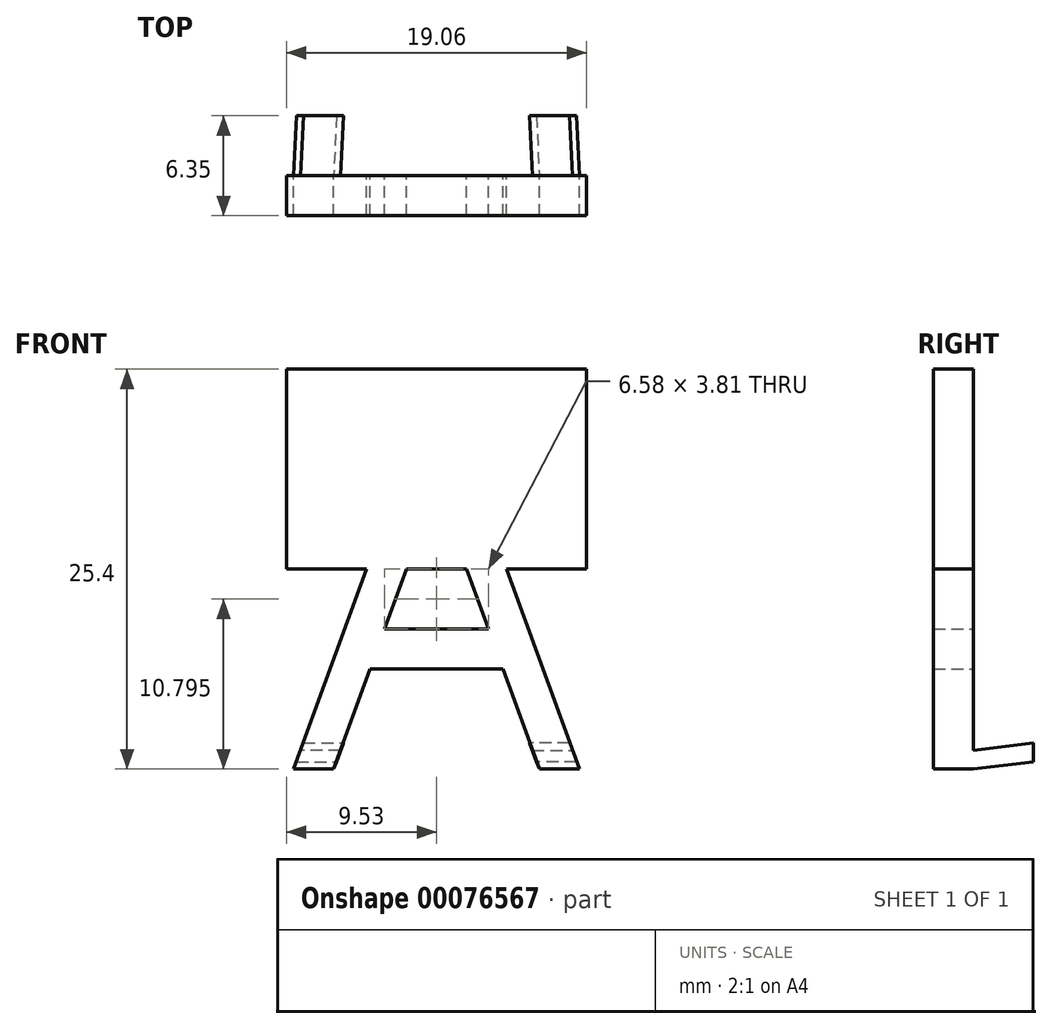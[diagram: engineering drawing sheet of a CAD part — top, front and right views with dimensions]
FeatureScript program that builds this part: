
annotation { "Feature Type Name" : "Feature", "Feature Type Description" : "" }
export const myFeature = defineFeature(function(context is Context, id is Id, definition is map)
    precondition{}
    {
        {
            var Q0;
            Q0=qCreatedBy(makeId("Front.planeOp"),FACE);
            var sketch = newSketch(context, id + "F0", { "sketchPlane" : qUnion([Q0])});
            skLineSegment(sketch, "E0.bottom", {"start": v(-9.52, -6.35) * mm, "end": v(-4.44, -6.35) * mm});
            skLineSegment(sketch, "E0.top", {"start": v(-9.53, 6.35) * mm, "end": v(9.52, 6.35) * mm});
            skLineSegment(sketch, "E0.left", {"start": v(-9.52, -6.35) * mm, "end": v(-9.53, 6.35) * mm});
            skLineSegment(sketch, "E0.right", {"start": v(9.53, -6.35) * mm, "end": v(9.52, 6.35) * mm});
            skPoint(sketch, "E0.middle", {"position": v(0, 0) * mm});
            skLineSegment(sketch, "E1", {"start": v(-4.44, -6.35) * mm, "end": v(-9.07, -19.05) * mm});
            skLineSegment(sketch, "E2", {"start": v(-9.07, -19.05) * mm, "end": v(-6.53, -19.05) * mm});
            skLineSegment(sketch, "E3", {"start": v(-6.53, -19.05) * mm, "end": v(-4.22, -12.7) * mm});
            skLineSegment(sketch, "E4", {"start": v(1.9, -6.35) * mm, "end": v(3.3, -10.16) * mm});
            skLineSegment(sketch, "E5", {"start": v(6.53, -19.05) * mm, "end": v(9.07, -19.05) * mm});
            skLineSegment(sketch, "E6", {"start": v(9.07, -19.05) * mm, "end": v(4.44, -6.35) * mm});
            skLineSegment(sketch, "E7", {"start": v(-3.3, -10.16) * mm, "end": v(3.3, -10.16) * mm});
            skLineSegment(sketch, "E8", {"start": v(-4.22, -12.7) * mm, "end": v(4.22, -12.7) * mm});
            skLineSegment(sketch, "E9.trimOffspring", {"start": v(-3.3, -10.16) * mm, "end": v(-1.9, -6.35) * mm});
            skLineSegment(sketch, "E10.trimOffspring", {"start": v(4.22, -12.7) * mm, "end": v(6.53, -19.05) * mm});
            skLineSegment(sketch, "E11.trimOffspring", {"start": v(-1.9, -6.35) * mm, "end": v(1.9, -6.35) * mm});
            skLineSegment(sketch, "E12.trimOffspring", {"start": v(4.44, -6.35) * mm, "end": v(9.53, -6.35) * mm});
            skSolve(sketch);
        }
        {
            var Q0;
            Q0 = qSketchRegion(id + "F0", true);
            extrude(context, id + "F1", {"entities" : qUnion([Q0]), "depth" : 2.54 * mm});
        }
        {
            var Q0;
            Q0=makeQuery(id+"F1.opExtrude","CAP_FACE",FACE,{"disambiguationData":[OSD([sQuery(id+"F0.wireOp",EDGE,"E0.bottom"),sQuery(id+"F0.wireOp",EDGE,"E0.top"),sQuery(id+"F0.wireOp",EDGE,"E0.left"),sQuery(id+"F0.wireOp",EDGE,"E0.right"),sQuery(id+"F0.wireOp",EDGE,"E1"),sQuery(id+"F0.wireOp",EDGE,"E2"),sQuery(id+"F0.wireOp",EDGE,"E3"),sQuery(id+"F0.wireOp",EDGE,"E4"),sQuery(id+"F0.wireOp",EDGE,"E5"),sQuery(id+"F0.wireOp",EDGE,"E6"),sQuery(id+"F0.wireOp",EDGE,"E7"),sQuery(id+"F0.wireOp",EDGE,"E8"),sQuery(id+"F0.wireOp",EDGE,"E9.trimOffspring"),sQuery(id+"F0.wireOp",EDGE,"E10.trimOffspring"),sQuery(id+"F0.wireOp",EDGE,"E11.trimOffspring"),sQuery(id+"F0.wireOp",EDGE,"E12.trimOffspring")])],"isStart":true});
            var sketch = newSketch(context, id + "F2", { "sketchPlane" : qUnion([Q0])});
            skLineSegment(sketch, "E13", {"start": v(-9.07, -19.05) * mm, "end": v(-6.53, -19.05) * mm});
            skLineSegment(sketch, "E14", {"start": v(-6.53, -19.05) * mm, "end": v(-6.1, -17.86) * mm});
            skLineSegment(sketch, "E15", {"start": v(-6.1, -17.86) * mm, "end": v(-8.63, -17.86) * mm});
            skLineSegment(sketch, "E16", {"start": v(-8.63, -17.86) * mm, "end": v(-9.07, -19.05) * mm});
            skLineSegment(sketch, "E17", {"start": v(6.1, -17.86) * mm, "end": v(8.63, -17.86) * mm});
            skLineSegment(sketch, "E18", {"start": v(8.63, -17.86) * mm, "end": v(9.07, -19.05) * mm});
            skLineSegment(sketch, "E19", {"start": v(9.07, -19.05) * mm, "end": v(6.53, -19.05) * mm});
            skLineSegment(sketch, "E20", {"start": v(6.53, -19.05) * mm, "end": v(6.1, -17.86) * mm});
            skSolve(sketch);
        }
        {
            var Q0;
            Q0=qCreatedBy(makeId("Front.planeOp"),FACE);
            cPlane(context, id + "F3", {"entities" : qUnion([Q0]), "cplaneType" : CPlaneType.OFFSET, "offset" : 3.8 * mm, "oppositeDirection" : true, "width" : 152.4 * mm, "height" : 152.4 * mm});
        }
        {
            var Q0;
            Q0=qCreatedBy(id+"F3.planeOp",FACE);
            var sketch = newSketch(context, id + "F4", { "sketchPlane" : qUnion([Q0])});
            skLineSegment(sketch, "E21", {"start": v(8.45, -17.38) * mm, "end": v(8.89, -18.58) * mm});
            skLineSegment(sketch, "E22", {"start": v(8.45, -17.38) * mm, "end": v(5.91, -17.38) * mm});
            skLineSegment(sketch, "E23", {"start": v(8.89, -18.58) * mm, "end": v(6.35, -18.58) * mm});
            skLineSegment(sketch, "E24", {"start": v(6.35, -18.58) * mm, "end": v(5.91, -17.38) * mm});
            skLineSegment(sketch, "E25.MirrorCS", {"start": v(-8.45, -17.38) * mm, "end": v(-8.89, -18.58) * mm});
            skLineSegment(sketch, "E26.MirrorCS", {"start": v(-8.45, -17.38) * mm, "end": v(-5.91, -17.38) * mm});
            skLineSegment(sketch, "E27.MirrorCS", {"start": v(-6.35, -18.58) * mm, "end": v(-5.91, -17.38) * mm});
            skLineSegment(sketch, "E28.MirrorCS", {"start": v(-8.89, -18.58) * mm, "end": v(-6.35, -18.58) * mm});
            skSolve(sketch);
        }
        {
            var Q1;
            Q1=makeQuery(id+"F4.imprint","IMPRINT",FACE,{"disambiguationData":[TD([[makeQuery(id+"F4.imprint","IMPRINT",EDGE,{"derivedFrom":sQuery(id+"F4.wireOp",EDGE,"E25.MirrorCS")}),1.0]])]});
            var Q2;
            Q2=makeQuery(id+"F2.imprint","IMPRINT",FACE,{"disambiguationData":[TD([[makeQuery(id+"F2.imprint","IMPRINT",EDGE,{"derivedFrom":sQuery(id+"F2.wireOp",EDGE,"E17")}),-1.0]])]});
            loft(context, id + "F5", {"operationType" : NewBodyOperationType.ADD, "sheetProfilesArray" : [{ "sheetProfileEntities" : qUnion([Q1]) }, { "sheetProfileEntities" : qUnion([Q2]) }]});
        }
        {
            var Q1;
            Q1=makeQuery(id+"F4.imprint","IMPRINT",FACE,{"disambiguationData":[TD([[makeQuery(id+"F4.imprint","IMPRINT",EDGE,{"derivedFrom":sQuery(id+"F4.wireOp",EDGE,"E21")}),-1.0]])]});
            var Q2;
            Q2=makeQuery(id+"F2.imprint","IMPRINT",FACE,{"disambiguationData":[TD([[makeQuery(id+"F2.imprint","IMPRINT",EDGE,{"derivedFrom":sQuery(id+"F2.wireOp",EDGE,"E13")}),-1.0]])]});
            loft(context, id + "F6", {"operationType" : NewBodyOperationType.ADD, "sheetProfilesArray" : [{ "sheetProfileEntities" : qUnion([Q1]) }, { "sheetProfileEntities" : qUnion([Q2]) }]});
        }
    });
